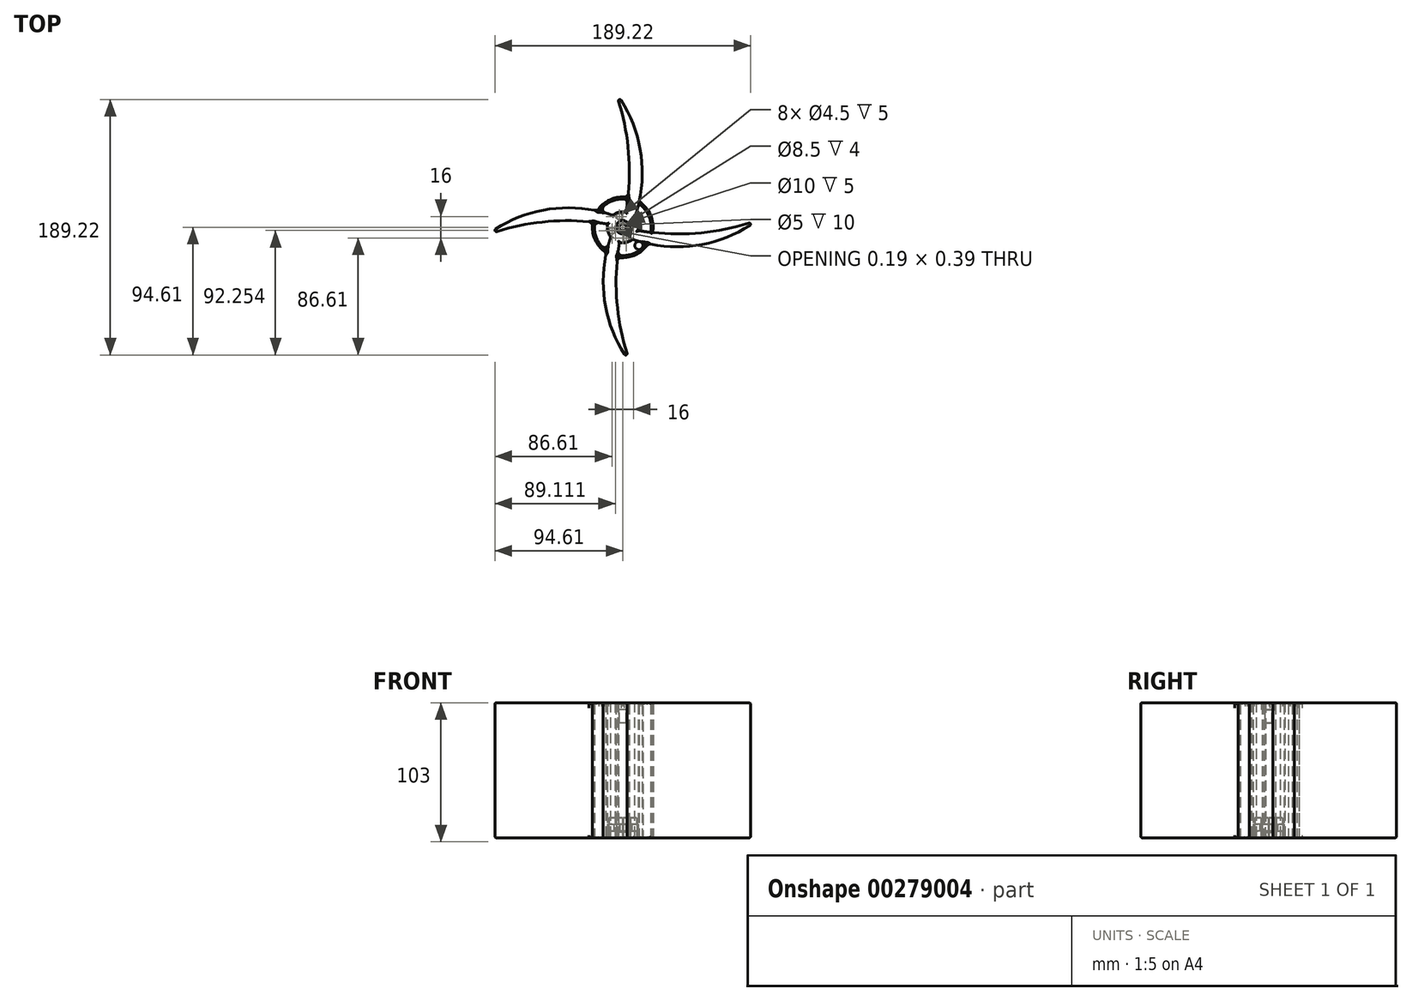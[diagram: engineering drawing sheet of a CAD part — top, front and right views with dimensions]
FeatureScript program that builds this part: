
annotation { "Feature Type Name" : "Feature", "Feature Type Description" : "" }
export const myFeature = defineFeature(function(context is Context, id is Id, definition is map)
    precondition{}
    {
        {
            assignVariable(context, id + "F0", {"name" : "BearingThickness", "anyValue" : 5});
        }
        {
            var Q0;
            Q0=qCreatedBy(makeId("Top.planeOp"),FACE);
            var sketch = newSketch(context, id + "F1", { "sketchPlane" : qUnion([Q0])});
            skCircle(sketch, "E0", {"center": v(0, 0) * mm, "radius": 2.5 * mm});
            skCircle(sketch, "E1", {"center": v(0, 0) * mm, "radius": 6 * mm});
            skPoint(sketch, "E2", {"position": v(-5.38, 100) * mm});
            skPoint(sketch, "E3", {"position": v(1.37, 5.84) * mm});
            skPoint(sketch, "E4.MirrorP", {"position": v(1.37, -5.84) * mm});
            skPoint(sketch, "E5", {"position": v(-6, 0) * mm});
            skPoint(sketch, "E6.MirrorP", {"position": v(6, 0) * mm});
            skArc(sketch, "E7", {"start": v(6, 0) * mm, "mid": v(14.14, 48) * mm, "end": v(-1.34, 94.15) * mm});
            skArc(sketch, "E8", {"start": v(1.37, 5.84) * mm, "mid": v(4.68, 49.86) * mm, "end": v(-3.13, 93.3) * mm});
            skArc(sketch, "E9.filletArc", {"start": v(-1.34, 94.15) * mm, "mid": v(-2.6, 94.52) * mm, "end": v(-3.13, 93.3) * mm});
            skCircle(sketch, "E10", {"center": v(0, 0) * mm, "radius": 11.5 * mm});
            skCircle(sketch, "E11", {"center": v(-8, -2.5) * mm, "radius": 2.25 * mm});
            skCircle(sketch, "E12", {"center": v(0, 0) * mm, "radius": 21 * mm});
            skCircle(sketch, "E13", {"center": v(0, 0) * mm, "radius": 22.5 * mm});
            skCircle(sketch, "E14.cCircle", {"center": v(-8, -2.5) * mm, "radius": 2.25 * mm, "construction": true});
            skLineSegment(sketch, "E14.0", {"start": v(-6.7, -4.75) * mm, "end": v(-9.3, -4.75) * mm});
            skLineSegment(sketch, "E14.3", {"start": v(-9.3, -0.25) * mm, "end": v(-6.7, -0.25) * mm});
            skLineSegment(sketch, "E14.4", {"start": v(-6.7, -0.25) * mm, "end": v(-5.4, -2.5) * mm});
            skLineSegment(sketch, "E14.5", {"start": v(-5.4, -2.5) * mm, "end": v(-6.7, -4.75) * mm});
            skPoint(sketch, "E14.0.midPoint", {"position": v(-8, -4.75) * mm});
            skLineSegment(sketch, "E15", {"start": v(-9.3, -4.75) * mm, "end": v(-22, -4.75) * mm});
            skLineSegment(sketch, "E16", {"start": v(-9.3, -0.25) * mm, "end": v(-22.5, -0.25) * mm});
            skSolve(sketch);
        }
        {
            var Q0;
            {var subQ0=sQuery(id+"F1.wireOp",EDGE,"E13");var subQ1=sQuery(id+"F1.wireOp",EDGE,"E7");var subQ2=makeQuery(id+"F1.imprint","INTERSECT",VERTEX,{"derivedFrom":[subQ1,subQ0]});Q0=makeQuery(id+"F1.imprint","IMPRINT",FACE,{"disambiguationData":[TD([[makeQuery(id+"F1.imprint","IMPRINT",EDGE,{"disambiguationData":[TD([[subQ2,1.0]])],"derivedFrom":subQ1}),-1.0]])]});}
            var Q1;
            Q1=makeQuery(id+"F1.imprint","IMPRINT",FACE,{"disambiguationData":[TD([[makeQuery(id+"F1.imprint","IMPRINT",EDGE,{"derivedFrom":sQuery(id+"F1.wireOp",EDGE,"E0")}),-1.0]])]});
            var Q2;
            {var subQ0=sQuery(id+"F1.wireOp",EDGE,"E16");var subQ1=sQuery(id+"F1.wireOp",EDGE,"E12");var subQ2=makeQuery(id+"F1.imprint","INTERSECT",VERTEX,{"derivedFrom":[subQ1,subQ0]});Q2=makeQuery(id+"F1.imprint","IMPRINT",FACE,{"disambiguationData":[TD([[makeQuery(id+"F1.imprint","IMPRINT",EDGE,{"disambiguationData":[TD([[subQ2,-1.0]])],"derivedFrom":subQ1}),-1.0]])]});}
            var Q3;
            {var subQ0=sQuery(id+"F1.wireOp",EDGE,"E13");var subQ1=sQuery(id+"F1.wireOp",EDGE,"E8");var subQ2=makeQuery(id+"F1.imprint","INTERSECT",VERTEX,{"derivedFrom":[subQ1,subQ0]});Q3=makeQuery(id+"F1.imprint","IMPRINT",FACE,{"disambiguationData":[TD([[makeQuery(id+"F1.imprint","IMPRINT",EDGE,{"disambiguationData":[TD([[subQ2,1.0]])],"derivedFrom":subQ1}),1.0]])]});}
            var Q4;
            {var subQ0=sQuery(id+"F1.wireOp",EDGE,"E13");var subQ1=sQuery(id+"F1.wireOp",EDGE,"E7");var subQ2=makeQuery(id+"F1.imprint","INTERSECT",VERTEX,{"derivedFrom":[subQ1,subQ0]});Q4=makeQuery(id+"F1.imprint","IMPRINT",FACE,{"disambiguationData":[TD([[makeQuery(id+"F1.imprint","IMPRINT",EDGE,{"disambiguationData":[TD([[subQ2,1.0]])],"derivedFrom":subQ1}),1.0]])]});}
            var Q5;
            {var subQ0=sQuery(id+"F1.wireOp",EDGE,"E7");var subQ1=sQuery(id+"F1.wireOp",EDGE,"E1");var subQ2=makeQuery(id+"F1.imprint","INTERSECT",VERTEX,{"derivedFrom":[subQ1,subQ0]});Q5=makeQuery(id+"F1.imprint","IMPRINT",FACE,{"disambiguationData":[TD([[makeQuery(id+"F1.imprint","IMPRINT",EDGE,{"disambiguationData":[TD([[subQ2,-1.0]])],"derivedFrom":subQ1}),-1.0]])]});}
            var Q6;
            {var subQ5=sQuery(id+"F1.wireOp",EDGE,"E16");var subQ6=sQuery(id+"F1.wireOp",EDGE,"E10");var subQ7=makeQuery(id+"F1.imprint","INTERSECT",VERTEX,{"derivedFrom":[subQ6,subQ5]});Q6=makeQuery(id+"F1.imprint","IMPRINT",FACE,{"disambiguationData":[TD([[makeQuery(id+"F1.imprint","IMPRINT",EDGE,{"disambiguationData":[TD([[subQ7,-1.0]])],"derivedFrom":subQ6}),1.0]])]});}
            var Q7;
            {var subQ0=sQuery(id+"F1.wireOp",EDGE,"E11");var subQ1=makeQuery(id+"F1.imprint","INTERSECT",VERTEX,{"derivedFrom":[subQ0,sQuery(id+"F1.wireOp",EDGE,"E14.3")]});Q7=makeQuery(id+"F1.imprint","IMPRINT",FACE,{"disambiguationData":[TD([[makeQuery(id+"F1.imprint","IMPRINT",EDGE,{"disambiguationData":[TD([[subQ1,1.0]])],"derivedFrom":subQ0}),1.0]])]});}
            var Q8;
            {var subQ0=sQuery(id+"F1.wireOp",EDGE,"E14.0");var subQ1=sQuery(id+"F1.wireOp",EDGE,"E11");var subQ2=makeQuery(id+"F1.imprint","INTERSECT",VERTEX,{"derivedFrom":[subQ1,subQ0]});Q8=makeQuery(id+"F1.imprint","IMPRINT",FACE,{"disambiguationData":[TD([[makeQuery(id+"F1.imprint","IMPRINT",EDGE,{"disambiguationData":[TD([[subQ2,-1.0]])],"derivedFrom":subQ1}),-1.0]])]});}
            var Q9;
            {var subQ0=sQuery(id+"F1.wireOp",EDGE,"E14.3");var subQ1=sQuery(id+"F1.wireOp",EDGE,"E11");var subQ2=makeQuery(id+"F1.imprint","INTERSECT",VERTEX,{"derivedFrom":[subQ1,subQ0]});Q9=makeQuery(id+"F1.imprint","IMPRINT",FACE,{"disambiguationData":[TD([[makeQuery(id+"F1.imprint","IMPRINT",EDGE,{"disambiguationData":[TD([[subQ2,1.0]])],"derivedFrom":subQ1}),-1.0]])]});}
            var Q10;
            {var subQ0=sQuery(id+"F1.wireOp",EDGE,"E14.4");var subQ1=sQuery(id+"F1.wireOp",EDGE,"E11");var subQ2=makeQuery(id+"F1.imprint","INTERSECT",VERTEX,{"derivedFrom":[subQ1,subQ0]});Q10=makeQuery(id+"F1.imprint","IMPRINT",FACE,{"disambiguationData":[TD([[makeQuery(id+"F1.imprint","IMPRINT",EDGE,{"disambiguationData":[TD([[subQ2,1.0]])],"derivedFrom":subQ1}),-1.0]])]});}
            var Q11;
            {var subQ11=sQuery(id+"F1.wireOp",EDGE,"E7");var subQ16=sQuery(id+"F1.wireOp",EDGE,"E1");var subQ17=makeQuery(id+"F1.imprint","INTERSECT",VERTEX,{"derivedFrom":[subQ16,subQ11]});Q11=makeQuery(id+"F1.imprint","IMPRINT",FACE,{"disambiguationData":[TD([[makeQuery(id+"F1.imprint","IMPRINT",EDGE,{"disambiguationData":[TD([[subQ17,1.0]])],"derivedFrom":subQ16}),-1.0]])]});}
            var Q12;
            {var subQ1=sQuery(id+"F1.wireOp",EDGE,"E8");var subQ5=sQuery(id+"F1.wireOp",EDGE,"E1");var subQ6=makeQuery(id+"F1.imprint","INTERSECT",VERTEX,{"derivedFrom":[subQ5,subQ1]});Q12=makeQuery(id+"F1.imprint","IMPRINT",FACE,{"disambiguationData":[TD([[makeQuery(id+"F1.imprint","IMPRINT",EDGE,{"disambiguationData":[TD([[subQ6,-1.0]])],"derivedFrom":subQ5}),-1.0]])]});}
            var Q13;
            Q13=makeQuery(id+"F1.imprint","IMPRINT",FACE,{"disambiguationData":[TD([[makeQuery(id+"F1.imprint","IMPRINT",EDGE,{"derivedFrom":sQuery(id+"F1.wireOp",EDGE,"E0")}),1.0]])]});
            extrude(context, id + "F2", {"entities" : qUnion([Q0, Q1, Q2, Q3, Q4, Q5, Q6, Q7, Q8, Q9, Q10, Q11, Q12, Q13]), "depth" : 100 * mm});
        }
        {
            var Q0;
            {var subQ0=sQuery(id+"F1.wireOp",EDGE,"E9.filletArc");Q0=makeQuery(id+"F1.imprint","IMPRINT",FACE,{"disambiguationData":[TD([[makeQuery(id+"F1.imprint","IMPRINT",EDGE,{"derivedFrom":subQ0}),1.0]])]});}
            var Q1;
            {var subQ0=sQuery(id+"F1.wireOp",EDGE,"E10");var subQ1=sQuery(id+"F1.wireOp",EDGE,"E7");var subQ2=makeQuery(id+"F1.imprint","INTERSECT",VERTEX,{"derivedFrom":[subQ1,subQ0]});Q1=makeQuery(id+"F1.imprint","IMPRINT",FACE,{"disambiguationData":[TD([[makeQuery(id+"F1.imprint","IMPRINT",EDGE,{"disambiguationData":[TD([[subQ2,-1.0]])],"derivedFrom":subQ1}),1.0]])]});}
            var Q2;
            {var subQ0=sQuery(id+"F1.wireOp",EDGE,"E7");var subQ1=sQuery(id+"F1.wireOp",EDGE,"E1");var subQ2=makeQuery(id+"F1.imprint","INTERSECT",VERTEX,{"derivedFrom":[subQ1,subQ0]});Q2=makeQuery(id+"F1.imprint","IMPRINT",FACE,{"disambiguationData":[TD([[makeQuery(id+"F1.imprint","IMPRINT",EDGE,{"disambiguationData":[TD([[subQ2,-1.0]])],"derivedFrom":subQ1}),-1.0]])]});}
            extrude(context, id + "F3", {"entities" : qUnion([Q0, Q1, Q2]), "depth" : 100 * mm});
        }
        {
            var Q0;
            Q0=makeQuery(id+"F3.opExtrude","SWEPT_BODY",BODY,{"disambiguationData":[OSD([sQuery(id+"F1.wireOp",EDGE,"E7"),sQuery(id+"F1.wireOp",EDGE,"E8"),sQuery(id+"F1.wireOp",EDGE,"E9.filletArc"),sQuery(id+"F1.wireOp",EDGE,"E13")])]});
            var Q1;
            Q1=makeQuery(id+"F3.opExtrude","SWEPT_BODY",BODY,{"disambiguationData":[OSD([sQuery(id+"F1.wireOp",EDGE,"E1"),sQuery(id+"F1.wireOp",EDGE,"E7"),sQuery(id+"F1.wireOp",EDGE,"E8"),sQuery(id+"F1.wireOp",EDGE,"E12")])]});
            var Q2;
            Q2=sQuery(id+"F1.wireOp",EDGE,"E0");
            circularPattern(context, id + "F4", {"operationType" : NewBodyOperationType.ADD, "entities" : qUnion([Q0, Q1]), "axis" : qUnion([Q2]), "angle" : 360 * degree, "instanceCount" : 4, "equalSpace" : true});
        }
        {
            var Q0;
            {var subQ0=sQuery(id+"F1.wireOp",EDGE,"E11");var subQ1=makeQuery(id+"F1.imprint","INTERSECT",VERTEX,{"derivedFrom":[subQ0,sQuery(id+"F1.wireOp",EDGE,"E14.3")]});Q0=makeQuery(id+"F1.imprint","IMPRINT",FACE,{"disambiguationData":[TD([[makeQuery(id+"F1.imprint","IMPRINT",EDGE,{"disambiguationData":[TD([[subQ1,1.0]])],"derivedFrom":subQ0}),1.0]])]});}
            extrude(context, id + "F5", {"entities" : qUnion([Q0]), "depth" : 15 * mm, "hasSecondDirection" : true, "secondDirectionOppositeDirection" : true, "secondDirectionDepth" : 15 * mm});
        }
        {
            var Q0;
            Q0=makeQuery(id+"F5.opExtrude","SWEPT_BODY",BODY,{"disambiguationData":[OSD([sQuery(id+"F1.wireOp",EDGE,"E11")])]});
            var Q1;
            Q1=makeQuery(id+"F5.opExtrude","SWEPT_BODY",BODY,{"disambiguationData":[OSD([sQuery(id+"F1.wireOp",EDGE,"E11")])]});
            var Q2;
            Q2=sQuery(id+"F1.wireOp",EDGE,"E0");
            circularPattern(context, id + "F6", {"operationType" : NewBodyOperationType.REMOVE, "entities" : qUnion([Q0, Q1]), "axis" : qUnion([Q2]), "angle" : 360 * degree, "instanceCount" : 4, "equalSpace" : true});
        }
        {
            var Q0;
            {var subQ5=sQuery(id+"F1.wireOp",EDGE,"E16");var subQ6=sQuery(id+"F1.wireOp",EDGE,"E10");var subQ7=makeQuery(id+"F1.imprint","INTERSECT",VERTEX,{"derivedFrom":[subQ6,subQ5]});Q0=makeQuery(id+"F1.imprint","IMPRINT",FACE,{"disambiguationData":[TD([[makeQuery(id+"F1.imprint","IMPRINT",EDGE,{"disambiguationData":[TD([[subQ7,-1.0]])],"derivedFrom":subQ6}),1.0]])]});}
            var Q1;
            {var subQ0=sQuery(id+"F1.wireOp",EDGE,"E14.4");var subQ1=sQuery(id+"F1.wireOp",EDGE,"E11");var subQ2=makeQuery(id+"F1.imprint","INTERSECT",VERTEX,{"derivedFrom":[subQ1,subQ0]});Q1=makeQuery(id+"F1.imprint","IMPRINT",FACE,{"disambiguationData":[TD([[makeQuery(id+"F1.imprint","IMPRINT",EDGE,{"disambiguationData":[TD([[subQ2,1.0]])],"derivedFrom":subQ1}),-1.0]])]});}
            var Q2;
            {var subQ0=sQuery(id+"F1.wireOp",EDGE,"E14.3");var subQ1=sQuery(id+"F1.wireOp",EDGE,"E11");var subQ2=makeQuery(id+"F1.imprint","INTERSECT",VERTEX,{"derivedFrom":[subQ1,subQ0]});Q2=makeQuery(id+"F1.imprint","IMPRINT",FACE,{"disambiguationData":[TD([[makeQuery(id+"F1.imprint","IMPRINT",EDGE,{"disambiguationData":[TD([[subQ2,1.0]])],"derivedFrom":subQ1}),-1.0]])]});}
            var Q3;
            {var subQ0=sQuery(id+"F1.wireOp",EDGE,"E14.0");var subQ1=sQuery(id+"F1.wireOp",EDGE,"E11");var subQ2=makeQuery(id+"F1.imprint","INTERSECT",VERTEX,{"derivedFrom":[subQ1,subQ0]});Q3=makeQuery(id+"F1.imprint","IMPRINT",FACE,{"disambiguationData":[TD([[makeQuery(id+"F1.imprint","IMPRINT",EDGE,{"disambiguationData":[TD([[subQ2,-1.0]])],"derivedFrom":subQ1}),-1.0]])]});}
            extrude(context, id + "F7", {"entities" : qUnion([Q0, Q1, Q2, Q3]), "depth" : 10 * mm, "hasSecondDirection" : true, "secondDirectionOppositeDirection" : false, "secondDirectionDepth" : 5 * mm});
        }
        {
            var Q0;
            Q0=makeQuery(id+"F7.opExtrude","SWEPT_BODY",BODY,{"disambiguationData":[OSD([sQuery(id+"F1.wireOp",EDGE,"E11"),sQuery(id+"F1.wireOp",EDGE,"E14.0"),sQuery(id+"F1.wireOp",EDGE,"E14.5")])]});
            var Q1;
            Q1=makeQuery(id+"F7.opExtrude","SWEPT_BODY",BODY,{"disambiguationData":[OSD([sQuery(id+"F1.wireOp",EDGE,"E11"),sQuery(id+"F1.wireOp",EDGE,"E14.4"),sQuery(id+"F1.wireOp",EDGE,"E14.5")])]});
            var Q2;
            Q2=makeQuery(id+"F7.opExtrude","SWEPT_BODY",BODY,{"disambiguationData":[OSD([sQuery(id+"F1.wireOp",EDGE,"E10"),sQuery(id+"F1.wireOp",EDGE,"E11"),sQuery(id+"F1.wireOp",EDGE,"E14.0"),sQuery(id+"F1.wireOp",EDGE,"E14.3"),sQuery(id+"F1.wireOp",EDGE,"E15"),sQuery(id+"F1.wireOp",EDGE,"E16")])]});
            var Q3;
            Q3=makeQuery(id+"F7.opExtrude","SWEPT_BODY",BODY,{"disambiguationData":[OSD([sQuery(id+"F1.wireOp",EDGE,"E11"),sQuery(id+"F1.wireOp",EDGE,"E14.3"),sQuery(id+"F1.wireOp",EDGE,"E14.4")])]});
            var Q4;
            Q4=sQuery(id+"F1.wireOp",EDGE,"E0");
            circularPattern(context, id + "F8", {"operationType" : NewBodyOperationType.REMOVE, "entities" : qUnion([Q0, Q1, Q2, Q3]), "axis" : qUnion([Q4]), "angle" : 360 * degree, "instanceCount" : 4, "equalSpace" : true});
        }
        {
            var Q0;
            {var subQ0=sQuery(id+"F1.wireOp",EDGE,"E8");Q0=makeQuery(id+"F4.opPattern","COPY",EDGE,{"derivedFrom":makeQuery(id+"F3.opExtrude","CAP_EDGE",EDGE,{"disambiguationData":[OSD([subQ0]),TDD([makeQuery(id+"F1.imprint","IMPRINT",EDGE,{"disambiguationData":[TD([[makeQuery(id+"F1.imprint","INTERSECT",VERTEX,{"derivedFrom":[subQ0,sQuery(id+"F1.wireOp",EDGE,"E9.filletArc")]}),1.0]])],"derivedFrom":subQ0})])],"isStart":true}),"instanceName":"2"});}
            var Q1;
            {var subQ0=sQuery(id+"F1.wireOp",EDGE,"E13");var subQ1=sQuery(id+"F1.wireOp",EDGE,"E9.filletArc");var subQ2=sQuery(id+"F1.wireOp",EDGE,"E8");Q1=makeQuery(id+"F4.boolean.opBoolean","SPLIT",EDGE,{"disambiguationData":[TD([makeQuery(id+"F4.opPattern","COPY",FACE,{"derivedFrom":makeQuery(id+"F3.opExtrude","SWEPT_FACE",FACE,{"disambiguationData":[OSD([subQ2]),TDD([makeQuery(id+"F1.imprint","IMPRINT",EDGE,{"disambiguationData":[TD([[makeQuery(id+"F1.imprint","INTERSECT",VERTEX,{"derivedFrom":[subQ2,subQ1]}),1.0]])],"derivedFrom":subQ2})])]}),"instanceName":"2"})])],"derivedFrom":makeQuery(id+"F2.opExtrude","CAP_EDGE",EDGE,{"disambiguationData":[OSD([subQ0])],"isStart":true})});}
            var Q2;
            {var subQ0=sQuery(id+"F1.wireOp",EDGE,"E7");Q2=makeQuery(id+"F4.opPattern","COPY",EDGE,{"derivedFrom":makeQuery(id+"F3.opExtrude","CAP_EDGE",EDGE,{"disambiguationData":[OSD([subQ0]),TDD([makeQuery(id+"F1.imprint","IMPRINT",EDGE,{"disambiguationData":[TD([[makeQuery(id+"F1.imprint","INTERSECT",VERTEX,{"derivedFrom":[subQ0,sQuery(id+"F1.wireOp",EDGE,"E9.filletArc")]}),1.0]])],"derivedFrom":subQ0})])],"isStart":true}),"instanceName":"3"});}
            var Q3;
            {var subQ0=sQuery(id+"F1.wireOp",EDGE,"E13");var subQ1=sQuery(id+"F1.wireOp",EDGE,"E9.filletArc");var subQ2=sQuery(id+"F1.wireOp",EDGE,"E8");Q3=makeQuery(id+"F4.boolean.opBoolean","SPLIT",EDGE,{"disambiguationData":[TD([makeQuery(id+"F3.opExtrude","SWEPT_FACE",FACE,{"disambiguationData":[OSD([subQ2]),TDD([makeQuery(id+"F1.imprint","IMPRINT",EDGE,{"disambiguationData":[TD([[makeQuery(id+"F1.imprint","INTERSECT",VERTEX,{"derivedFrom":[subQ2,subQ1]}),1.0]])],"derivedFrom":subQ2})])]})])],"derivedFrom":makeQuery(id+"F2.opExtrude","CAP_EDGE",EDGE,{"disambiguationData":[OSD([subQ0])],"isStart":true})});}
            var Q4;
            {var subQ0=sQuery(id+"F1.wireOp",EDGE,"E9.filletArc");var subQ2=sQuery(id+"F1.wireOp",EDGE,"E13");var subQ3=sQuery(id+"F1.wireOp",EDGE,"E8");Q4=makeQuery(id+"F4.boolean.opBoolean","SPLIT",EDGE,{"disambiguationData":[TD([makeQuery(id+"F4.opPattern","COPY",FACE,{"derivedFrom":makeQuery(id+"F3.opExtrude","SWEPT_FACE",FACE,{"disambiguationData":[OSD([subQ3]),TDD([makeQuery(id+"F1.imprint","IMPRINT",EDGE,{"disambiguationData":[TD([[makeQuery(id+"F1.imprint","INTERSECT",VERTEX,{"derivedFrom":[subQ3,subQ0]}),1.0]])],"derivedFrom":subQ3})])]}),"instanceName":"1"})])],"derivedFrom":makeQuery(id+"F2.opExtrude","CAP_EDGE",EDGE,{"disambiguationData":[OSD([subQ2])],"isStart":true})});}
            var Q5;
            {var subQ0=sQuery(id+"F1.wireOp",EDGE,"E13");var subQ1=sQuery(id+"F1.wireOp",EDGE,"E9.filletArc");var subQ3=sQuery(id+"F1.wireOp",EDGE,"E7");Q5=makeQuery(id+"F4.boolean.opBoolean","SPLIT",EDGE,{"disambiguationData":[TD([makeQuery(id+"F3.opExtrude","SWEPT_FACE",FACE,{"disambiguationData":[OSD([subQ3]),TDD([makeQuery(id+"F1.imprint","IMPRINT",EDGE,{"disambiguationData":[TD([[makeQuery(id+"F1.imprint","INTERSECT",VERTEX,{"derivedFrom":[subQ3,subQ1]}),1.0]])],"derivedFrom":subQ3})])]})])],"derivedFrom":makeQuery(id+"F2.opExtrude","CAP_EDGE",EDGE,{"disambiguationData":[OSD([subQ0])],"isStart":true})});}
            var Q6;
            {var subQ0=sQuery(id+"F1.wireOp",EDGE,"E8");Q6=makeQuery(id+"F3.opExtrude","CAP_EDGE",EDGE,{"disambiguationData":[OSD([subQ0]),TDD([makeQuery(id+"F1.imprint","IMPRINT",EDGE,{"disambiguationData":[TD([[makeQuery(id+"F1.imprint","INTERSECT",VERTEX,{"derivedFrom":[subQ0,sQuery(id+"F1.wireOp",EDGE,"E9.filletArc")]}),1.0]])],"derivedFrom":subQ0})])],"isStart":true});}
            var Q7;
            {var subQ0=sQuery(id+"F1.wireOp",EDGE,"E8");Q7=makeQuery(id+"F4.opPattern","COPY",EDGE,{"derivedFrom":makeQuery(id+"F3.opExtrude","CAP_EDGE",EDGE,{"disambiguationData":[OSD([subQ0]),TDD([makeQuery(id+"F1.imprint","IMPRINT",EDGE,{"disambiguationData":[TD([[makeQuery(id+"F1.imprint","INTERSECT",VERTEX,{"derivedFrom":[subQ0,sQuery(id+"F1.wireOp",EDGE,"E9.filletArc")]}),1.0]])],"derivedFrom":subQ0})])],"isStart":true}),"instanceName":"1"});}
            var Q8;
            {var subQ0=sQuery(id+"F1.wireOp",EDGE,"E7");var subQ1=makeQuery(id+"F1.imprint","INTERSECT",VERTEX,{"derivedFrom":[subQ0,sQuery(id+"F1.wireOp",EDGE,"E10")]});Q8=makeQuery(id+"F4.opPattern","COPY",EDGE,{"derivedFrom":makeQuery(id+"F3.opExtrude","CAP_EDGE",EDGE,{"disambiguationData":[OSD([subQ0]),TDD([makeQuery(id+"F1.imprint","IMPRINT",EDGE,{"disambiguationData":[TD([[makeQuery(id+"F1.imprint","INTERSECT",VERTEX,{"derivedFrom":[sQuery(id+"F1.wireOp",EDGE,"E1"),subQ0]}),-1.0]])],"derivedFrom":subQ0}),makeQuery(id+"F1.imprint","IMPRINT",EDGE,{"disambiguationData":[TD([[subQ1,-1.0]])],"derivedFrom":subQ0})])],"isStart":true}),"instanceName":"1"});}
            var Q9;
            {var subQ0=sQuery(id+"F1.wireOp",EDGE,"E8");var subQ1=makeQuery(id+"F1.imprint","INTERSECT",VERTEX,{"derivedFrom":[subQ0,sQuery(id+"F1.wireOp",EDGE,"E10")]});Q9=makeQuery(id+"F4.opPattern","COPY",EDGE,{"derivedFrom":makeQuery(id+"F3.opExtrude","CAP_EDGE",EDGE,{"disambiguationData":[OSD([subQ0]),TDD([makeQuery(id+"F1.imprint","IMPRINT",EDGE,{"disambiguationData":[TD([[makeQuery(id+"F1.imprint","INTERSECT",VERTEX,{"derivedFrom":[sQuery(id+"F1.wireOp",EDGE,"E1"),subQ0]}),-1.0]])],"derivedFrom":subQ0}),makeQuery(id+"F1.imprint","IMPRINT",EDGE,{"disambiguationData":[TD([[subQ1,-1.0]])],"derivedFrom":subQ0})])],"isStart":true}),"instanceName":"1"});}
            var Q10;
            {var subQ0=sQuery(id+"F1.wireOp",EDGE,"E7");var subQ1=makeQuery(id+"F1.imprint","INTERSECT",VERTEX,{"derivedFrom":[subQ0,sQuery(id+"F1.wireOp",EDGE,"E10")]});Q10=makeQuery(id+"F4.opPattern","COPY",EDGE,{"derivedFrom":makeQuery(id+"F3.opExtrude","CAP_EDGE",EDGE,{"disambiguationData":[OSD([subQ0]),TDD([makeQuery(id+"F1.imprint","IMPRINT",EDGE,{"disambiguationData":[TD([[makeQuery(id+"F1.imprint","INTERSECT",VERTEX,{"derivedFrom":[sQuery(id+"F1.wireOp",EDGE,"E1"),subQ0]}),-1.0]])],"derivedFrom":subQ0}),makeQuery(id+"F1.imprint","IMPRINT",EDGE,{"disambiguationData":[TD([[subQ1,-1.0]])],"derivedFrom":subQ0})])],"isStart":true}),"instanceName":"2"});}
            var Q11;
            {var subQ0=sQuery(id+"F1.wireOp",EDGE,"E8");var subQ1=makeQuery(id+"F1.imprint","INTERSECT",VERTEX,{"derivedFrom":[subQ0,sQuery(id+"F1.wireOp",EDGE,"E10")]});Q11=makeQuery(id+"F4.opPattern","COPY",EDGE,{"derivedFrom":makeQuery(id+"F3.opExtrude","CAP_EDGE",EDGE,{"disambiguationData":[OSD([subQ0]),TDD([makeQuery(id+"F1.imprint","IMPRINT",EDGE,{"disambiguationData":[TD([[makeQuery(id+"F1.imprint","INTERSECT",VERTEX,{"derivedFrom":[sQuery(id+"F1.wireOp",EDGE,"E1"),subQ0]}),-1.0]])],"derivedFrom":subQ0}),makeQuery(id+"F1.imprint","IMPRINT",EDGE,{"disambiguationData":[TD([[subQ1,-1.0]])],"derivedFrom":subQ0})])],"isStart":true}),"instanceName":"2"});}
            var Q12;
            {var subQ0=sQuery(id+"F1.wireOp",EDGE,"E7");var subQ1=makeQuery(id+"F1.imprint","INTERSECT",VERTEX,{"derivedFrom":[subQ0,sQuery(id+"F1.wireOp",EDGE,"E10")]});Q12=makeQuery(id+"F4.opPattern","COPY",EDGE,{"derivedFrom":makeQuery(id+"F3.opExtrude","CAP_EDGE",EDGE,{"disambiguationData":[OSD([subQ0]),TDD([makeQuery(id+"F1.imprint","IMPRINT",EDGE,{"disambiguationData":[TD([[makeQuery(id+"F1.imprint","INTERSECT",VERTEX,{"derivedFrom":[sQuery(id+"F1.wireOp",EDGE,"E1"),subQ0]}),-1.0]])],"derivedFrom":subQ0}),makeQuery(id+"F1.imprint","IMPRINT",EDGE,{"disambiguationData":[TD([[subQ1,-1.0]])],"derivedFrom":subQ0})])],"isStart":true}),"instanceName":"3"});}
            var Q13;
            {var subQ0=sQuery(id+"F1.wireOp",EDGE,"E8");var subQ1=makeQuery(id+"F1.imprint","INTERSECT",VERTEX,{"derivedFrom":[subQ0,sQuery(id+"F1.wireOp",EDGE,"E10")]});Q13=makeQuery(id+"F4.opPattern","COPY",EDGE,{"derivedFrom":makeQuery(id+"F3.opExtrude","CAP_EDGE",EDGE,{"disambiguationData":[OSD([subQ0]),TDD([makeQuery(id+"F1.imprint","IMPRINT",EDGE,{"disambiguationData":[TD([[makeQuery(id+"F1.imprint","INTERSECT",VERTEX,{"derivedFrom":[sQuery(id+"F1.wireOp",EDGE,"E1"),subQ0]}),-1.0]])],"derivedFrom":subQ0}),makeQuery(id+"F1.imprint","IMPRINT",EDGE,{"disambiguationData":[TD([[subQ1,-1.0]])],"derivedFrom":subQ0})])],"isStart":true}),"instanceName":"3"});}
            var Q14;
            {var subQ0=sQuery(id+"F1.wireOp",EDGE,"E7");var subQ1=makeQuery(id+"F1.imprint","INTERSECT",VERTEX,{"derivedFrom":[subQ0,sQuery(id+"F1.wireOp",EDGE,"E10")]});Q14=makeQuery(id+"F3.opExtrude","CAP_EDGE",EDGE,{"disambiguationData":[OSD([subQ0]),TDD([makeQuery(id+"F1.imprint","IMPRINT",EDGE,{"disambiguationData":[TD([[makeQuery(id+"F1.imprint","INTERSECT",VERTEX,{"derivedFrom":[sQuery(id+"F1.wireOp",EDGE,"E1"),subQ0]}),-1.0]])],"derivedFrom":subQ0}),makeQuery(id+"F1.imprint","IMPRINT",EDGE,{"disambiguationData":[TD([[subQ1,-1.0]])],"derivedFrom":subQ0})])],"isStart":true});}
            var Q15;
            {var subQ0=sQuery(id+"F1.wireOp",EDGE,"E8");var subQ1=makeQuery(id+"F1.imprint","INTERSECT",VERTEX,{"derivedFrom":[subQ0,sQuery(id+"F1.wireOp",EDGE,"E10")]});Q15=makeQuery(id+"F3.opExtrude","CAP_EDGE",EDGE,{"disambiguationData":[OSD([subQ0]),TDD([makeQuery(id+"F1.imprint","IMPRINT",EDGE,{"disambiguationData":[TD([[makeQuery(id+"F1.imprint","INTERSECT",VERTEX,{"derivedFrom":[sQuery(id+"F1.wireOp",EDGE,"E1"),subQ0]}),-1.0]])],"derivedFrom":subQ0}),makeQuery(id+"F1.imprint","IMPRINT",EDGE,{"disambiguationData":[TD([[subQ1,-1.0]])],"derivedFrom":subQ0})])],"isStart":true});}
            var Q16;
            {var subQ1=sQuery(id+"F1.wireOp",EDGE,"E8");var subQ4=sQuery(id+"F1.wireOp",EDGE,"E10");var subQ7=sQuery(id+"F1.wireOp",EDGE,"E1");var subQ8=makeQuery(id+"F1.imprint","INTERSECT",VERTEX,{"derivedFrom":[subQ1,subQ4]});Q16=makeQuery(id+"F4.boolean.opBoolean","SPLIT",EDGE,{"disambiguationData":[TD([makeQuery(id+"F3.opExtrude","SWEPT_FACE",FACE,{"disambiguationData":[OSD([subQ1]),TDD([makeQuery(id+"F1.imprint","IMPRINT",EDGE,{"disambiguationData":[TD([[makeQuery(id+"F1.imprint","INTERSECT",VERTEX,{"derivedFrom":[subQ7,subQ1]}),-1.0]])],"derivedFrom":subQ1}),makeQuery(id+"F1.imprint","IMPRINT",EDGE,{"disambiguationData":[TD([[subQ8,-1.0]])],"derivedFrom":subQ1})])]})])],"derivedFrom":makeQuery(id+"F2.opExtrude","CAP_EDGE",EDGE,{"disambiguationData":[OSD([subQ4])],"isStart":true})});}
            var Q17;
            {var subQ2=sQuery(id+"F1.wireOp",EDGE,"E7");var subQ4=sQuery(id+"F1.wireOp",EDGE,"E10");var subQ5=makeQuery(id+"F1.imprint","INTERSECT",VERTEX,{"derivedFrom":[subQ2,subQ4]});var subQ7=sQuery(id+"F1.wireOp",EDGE,"E1");Q17=makeQuery(id+"F4.boolean.opBoolean","SPLIT",EDGE,{"disambiguationData":[TD([makeQuery(id+"F3.opExtrude","SWEPT_FACE",FACE,{"disambiguationData":[OSD([subQ2]),TDD([makeQuery(id+"F1.imprint","IMPRINT",EDGE,{"disambiguationData":[TD([[makeQuery(id+"F1.imprint","INTERSECT",VERTEX,{"derivedFrom":[subQ7,subQ2]}),-1.0]])],"derivedFrom":subQ2}),makeQuery(id+"F1.imprint","IMPRINT",EDGE,{"disambiguationData":[TD([[subQ5,-1.0]])],"derivedFrom":subQ2})])]})])],"derivedFrom":makeQuery(id+"F2.opExtrude","CAP_EDGE",EDGE,{"disambiguationData":[OSD([subQ4])],"isStart":true})});}
            var Q18;
            {var subQ0=sQuery(id+"F1.wireOp",EDGE,"E10");var subQ1=sQuery(id+"F1.wireOp",EDGE,"E8");var subQ2=makeQuery(id+"F1.imprint","INTERSECT",VERTEX,{"derivedFrom":[subQ1,subQ0]});var subQ4=sQuery(id+"F1.wireOp",EDGE,"E1");Q18=makeQuery(id+"F4.boolean.opBoolean","SPLIT",EDGE,{"disambiguationData":[TD([makeQuery(id+"F4.opPattern","COPY",FACE,{"derivedFrom":makeQuery(id+"F3.opExtrude","SWEPT_FACE",FACE,{"disambiguationData":[OSD([subQ1]),TDD([makeQuery(id+"F1.imprint","IMPRINT",EDGE,{"disambiguationData":[TD([[makeQuery(id+"F1.imprint","INTERSECT",VERTEX,{"derivedFrom":[subQ4,subQ1]}),-1.0]])],"derivedFrom":subQ1}),makeQuery(id+"F1.imprint","IMPRINT",EDGE,{"disambiguationData":[TD([[subQ2,-1.0]])],"derivedFrom":subQ1})])]}),"instanceName":"2"})])],"derivedFrom":makeQuery(id+"F2.opExtrude","CAP_EDGE",EDGE,{"disambiguationData":[OSD([subQ0])],"isStart":true})});}
            var Q19;
            {var subQ1=sQuery(id+"F1.wireOp",EDGE,"E8");var subQ4=sQuery(id+"F1.wireOp",EDGE,"E10");var subQ7=sQuery(id+"F1.wireOp",EDGE,"E1");var subQ9=makeQuery(id+"F1.imprint","INTERSECT",VERTEX,{"derivedFrom":[subQ1,subQ4]});Q19=makeQuery(id+"F4.boolean.opBoolean","SPLIT",EDGE,{"disambiguationData":[TD([makeQuery(id+"F4.opPattern","COPY",FACE,{"derivedFrom":makeQuery(id+"F3.opExtrude","SWEPT_FACE",FACE,{"disambiguationData":[OSD([subQ1]),TDD([makeQuery(id+"F1.imprint","IMPRINT",EDGE,{"disambiguationData":[TD([[makeQuery(id+"F1.imprint","INTERSECT",VERTEX,{"derivedFrom":[subQ7,subQ1]}),-1.0]])],"derivedFrom":subQ1}),makeQuery(id+"F1.imprint","IMPRINT",EDGE,{"disambiguationData":[TD([[subQ9,-1.0]])],"derivedFrom":subQ1})])]}),"instanceName":"1"})])],"derivedFrom":makeQuery(id+"F2.opExtrude","CAP_EDGE",EDGE,{"disambiguationData":[OSD([subQ4])],"isStart":true})});}
            var Q20;
            Q20=makeQuery(id+"F8.boolean.opBoolean","COPY",EDGE,{"derivedFrom":makeQuery(id+"F8.opPattern","COPY",EDGE,{"derivedFrom":makeQuery(id+"F7.opExtrude","SWEPT_EDGE",EDGE,{"disambiguationData":[OSD([sQuery(id+"F1.wireOp",EDGE,"E10"),sQuery(id+"F1.wireOp",EDGE,"E16")])]}),"instanceName":"2"})});
            var Q21;
            Q21=makeQuery(id+"F8.boolean.opBoolean","COPY",EDGE,{"derivedFrom":makeQuery(id+"F8.opPattern","COPY",EDGE,{"derivedFrom":makeQuery(id+"F7.opExtrude","CAP_EDGE",EDGE,{"disambiguationData":[OSD([sQuery(id+"F1.wireOp",EDGE,"E10")])],"isStart":false}),"instanceName":"2"})});
            var Q22;
            Q22=makeQuery(id+"F8.boolean.opBoolean","COPY",EDGE,{"derivedFrom":makeQuery(id+"F8.opPattern","COPY",EDGE,{"derivedFrom":makeQuery(id+"F7.opExtrude","SWEPT_EDGE",EDGE,{"disambiguationData":[OSD([sQuery(id+"F1.wireOp",EDGE,"E10"),sQuery(id+"F1.wireOp",EDGE,"E15")])]}),"instanceName":"2"})});
            var Q23;
            Q23=makeQuery(id+"F8.boolean.opBoolean","COPY",EDGE,{"derivedFrom":makeQuery(id+"F8.opPattern","COPY",EDGE,{"derivedFrom":makeQuery(id+"F7.opExtrude","SWEPT_EDGE",EDGE,{"disambiguationData":[OSD([sQuery(id+"F1.wireOp",EDGE,"E10"),sQuery(id+"F1.wireOp",EDGE,"E15")])]}),"instanceName":"3"})});
            var Q24;
            Q24=makeQuery(id+"F8.boolean.opBoolean","COPY",EDGE,{"derivedFrom":makeQuery(id+"F8.opPattern","COPY",EDGE,{"derivedFrom":makeQuery(id+"F7.opExtrude","SWEPT_EDGE",EDGE,{"disambiguationData":[OSD([sQuery(id+"F1.wireOp",EDGE,"E10"),sQuery(id+"F1.wireOp",EDGE,"E16")])]}),"instanceName":"3"})});
            var Q25;
            Q25=makeQuery(id+"F8.boolean.opBoolean","COPY",EDGE,{"derivedFrom":makeQuery(id+"F8.opPattern","COPY",EDGE,{"derivedFrom":makeQuery(id+"F7.opExtrude","CAP_EDGE",EDGE,{"disambiguationData":[OSD([sQuery(id+"F1.wireOp",EDGE,"E10")])],"isStart":false}),"instanceName":"3"})});
            var Q26;
            Q26=makeQuery(id+"F8.boolean.opBoolean","COPY",EDGE,{"derivedFrom":makeQuery(id+"F7.opExtrude","CAP_EDGE",EDGE,{"disambiguationData":[OSD([sQuery(id+"F1.wireOp",EDGE,"E10")])],"isStart":false})});
            var Q27;
            Q27=makeQuery(id+"F8.boolean.opBoolean","COPY",EDGE,{"derivedFrom":makeQuery(id+"F7.opExtrude","SWEPT_EDGE",EDGE,{"disambiguationData":[OSD([sQuery(id+"F1.wireOp",EDGE,"E10"),sQuery(id+"F1.wireOp",EDGE,"E15")])]})});
            var Q28;
            Q28=makeQuery(id+"F8.boolean.opBoolean","COPY",EDGE,{"derivedFrom":makeQuery(id+"F7.opExtrude","SWEPT_EDGE",EDGE,{"disambiguationData":[OSD([sQuery(id+"F1.wireOp",EDGE,"E10"),sQuery(id+"F1.wireOp",EDGE,"E16")])]})});
            var Q29;
            Q29=makeQuery(id+"F8.boolean.opBoolean","COPY",EDGE,{"derivedFrom":makeQuery(id+"F8.opPattern","COPY",EDGE,{"derivedFrom":makeQuery(id+"F7.opExtrude","CAP_EDGE",EDGE,{"disambiguationData":[OSD([sQuery(id+"F1.wireOp",EDGE,"E10")])],"isStart":false}),"instanceName":"1"})});
            var Q30;
            Q30=makeQuery(id+"F8.boolean.opBoolean","COPY",EDGE,{"derivedFrom":makeQuery(id+"F8.opPattern","COPY",EDGE,{"derivedFrom":makeQuery(id+"F7.opExtrude","SWEPT_EDGE",EDGE,{"disambiguationData":[OSD([sQuery(id+"F1.wireOp",EDGE,"E10"),sQuery(id+"F1.wireOp",EDGE,"E15")])]}),"instanceName":"1"})});
            var Q31;
            Q31=makeQuery(id+"F8.boolean.opBoolean","COPY",EDGE,{"derivedFrom":makeQuery(id+"F8.opPattern","COPY",EDGE,{"derivedFrom":makeQuery(id+"F7.opExtrude","SWEPT_EDGE",EDGE,{"disambiguationData":[OSD([sQuery(id+"F1.wireOp",EDGE,"E10"),sQuery(id+"F1.wireOp",EDGE,"E16")])]}),"instanceName":"1"})});
            var Q32;
            {var subQ0=sQuery(id+"F1.wireOp",EDGE,"E8");Q32=makeQuery(id+"F4.opPattern","COPY",EDGE,{"derivedFrom":makeQuery(id+"F3.opExtrude","CAP_EDGE",EDGE,{"disambiguationData":[OSD([subQ0]),TDD([makeQuery(id+"F1.imprint","IMPRINT",EDGE,{"disambiguationData":[TD([[makeQuery(id+"F1.imprint","INTERSECT",VERTEX,{"derivedFrom":[subQ0,sQuery(id+"F1.wireOp",EDGE,"E9.filletArc")]}),1.0]])],"derivedFrom":subQ0})])],"isStart":false}),"instanceName":"2"});}
            var Q33;
            {var subQ0=sQuery(id+"F1.wireOp",EDGE,"E7");Q33=makeQuery(id+"F4.opPattern","COPY",EDGE,{"derivedFrom":makeQuery(id+"F3.opExtrude","CAP_EDGE",EDGE,{"disambiguationData":[OSD([subQ0]),TDD([makeQuery(id+"F1.imprint","IMPRINT",EDGE,{"disambiguationData":[TD([[makeQuery(id+"F1.imprint","INTERSECT",VERTEX,{"derivedFrom":[subQ0,sQuery(id+"F1.wireOp",EDGE,"E9.filletArc")]}),1.0]])],"derivedFrom":subQ0})])],"isStart":false}),"instanceName":"1"});}
            var Q34;
            {var subQ0=sQuery(id+"F1.wireOp",EDGE,"E7");Q34=makeQuery(id+"F3.opExtrude","CAP_EDGE",EDGE,{"disambiguationData":[OSD([subQ0]),TDD([makeQuery(id+"F1.imprint","IMPRINT",EDGE,{"disambiguationData":[TD([[makeQuery(id+"F1.imprint","INTERSECT",VERTEX,{"derivedFrom":[subQ0,sQuery(id+"F1.wireOp",EDGE,"E9.filletArc")]}),1.0]])],"derivedFrom":subQ0})])],"isStart":false});}
            var Q35;
            {var subQ0=sQuery(id+"F1.wireOp",EDGE,"E7");Q35=makeQuery(id+"F4.opPattern","COPY",EDGE,{"derivedFrom":makeQuery(id+"F3.opExtrude","CAP_EDGE",EDGE,{"disambiguationData":[OSD([subQ0]),TDD([makeQuery(id+"F1.imprint","IMPRINT",EDGE,{"disambiguationData":[TD([[makeQuery(id+"F1.imprint","INTERSECT",VERTEX,{"derivedFrom":[subQ0,sQuery(id+"F1.wireOp",EDGE,"E9.filletArc")]}),1.0]])],"derivedFrom":subQ0})])],"isStart":false}),"instanceName":"3"});}
            var Q36;
            {var subQ0=sQuery(id+"F1.wireOp",EDGE,"E13");var subQ1=sQuery(id+"F1.wireOp",EDGE,"E9.filletArc");var subQ3=sQuery(id+"F1.wireOp",EDGE,"E7");Q36=makeQuery(id+"F4.boolean.opBoolean","SPLIT",EDGE,{"disambiguationData":[TD([makeQuery(id+"F3.opExtrude","SWEPT_FACE",FACE,{"disambiguationData":[OSD([subQ3]),TDD([makeQuery(id+"F1.imprint","IMPRINT",EDGE,{"disambiguationData":[TD([[makeQuery(id+"F1.imprint","INTERSECT",VERTEX,{"derivedFrom":[subQ3,subQ1]}),1.0]])],"derivedFrom":subQ3})])]})])],"derivedFrom":makeQuery(id+"F2.opExtrude","CAP_EDGE",EDGE,{"disambiguationData":[OSD([subQ0])],"isStart":false})});}
            var Q37;
            {var subQ0=sQuery(id+"F1.wireOp",EDGE,"E13");var subQ1=sQuery(id+"F1.wireOp",EDGE,"E9.filletArc");var subQ2=sQuery(id+"F1.wireOp",EDGE,"E8");Q37=makeQuery(id+"F4.boolean.opBoolean","SPLIT",EDGE,{"disambiguationData":[TD([makeQuery(id+"F4.opPattern","COPY",FACE,{"derivedFrom":makeQuery(id+"F3.opExtrude","SWEPT_FACE",FACE,{"disambiguationData":[OSD([subQ2]),TDD([makeQuery(id+"F1.imprint","IMPRINT",EDGE,{"disambiguationData":[TD([[makeQuery(id+"F1.imprint","INTERSECT",VERTEX,{"derivedFrom":[subQ2,subQ1]}),1.0]])],"derivedFrom":subQ2})])]}),"instanceName":"2"})])],"derivedFrom":makeQuery(id+"F2.opExtrude","CAP_EDGE",EDGE,{"disambiguationData":[OSD([subQ0])],"isStart":false})});}
            var Q38;
            {var subQ0=sQuery(id+"F1.wireOp",EDGE,"E9.filletArc");var subQ2=sQuery(id+"F1.wireOp",EDGE,"E13");var subQ3=sQuery(id+"F1.wireOp",EDGE,"E8");Q38=makeQuery(id+"F4.boolean.opBoolean","SPLIT",EDGE,{"disambiguationData":[TD([makeQuery(id+"F4.opPattern","COPY",FACE,{"derivedFrom":makeQuery(id+"F3.opExtrude","SWEPT_FACE",FACE,{"disambiguationData":[OSD([subQ3]),TDD([makeQuery(id+"F1.imprint","IMPRINT",EDGE,{"disambiguationData":[TD([[makeQuery(id+"F1.imprint","INTERSECT",VERTEX,{"derivedFrom":[subQ3,subQ0]}),1.0]])],"derivedFrom":subQ3})])]}),"instanceName":"1"})])],"derivedFrom":makeQuery(id+"F2.opExtrude","CAP_EDGE",EDGE,{"disambiguationData":[OSD([subQ2])],"isStart":false})});}
            var Q39;
            {var subQ0=sQuery(id+"F1.wireOp",EDGE,"E13");var subQ1=sQuery(id+"F1.wireOp",EDGE,"E9.filletArc");var subQ2=sQuery(id+"F1.wireOp",EDGE,"E8");Q39=makeQuery(id+"F4.boolean.opBoolean","SPLIT",EDGE,{"disambiguationData":[TD([makeQuery(id+"F3.opExtrude","SWEPT_FACE",FACE,{"disambiguationData":[OSD([subQ2]),TDD([makeQuery(id+"F1.imprint","IMPRINT",EDGE,{"disambiguationData":[TD([[makeQuery(id+"F1.imprint","INTERSECT",VERTEX,{"derivedFrom":[subQ2,subQ1]}),1.0]])],"derivedFrom":subQ2})])]})])],"derivedFrom":makeQuery(id+"F2.opExtrude","CAP_EDGE",EDGE,{"disambiguationData":[OSD([subQ0])],"isStart":false})});}
            var Q40;
            {var subQ2=sQuery(id+"F1.wireOp",EDGE,"E7");var subQ4=sQuery(id+"F1.wireOp",EDGE,"E10");var subQ5=sQuery(id+"F1.wireOp",EDGE,"E12");var subQ6=sQuery(id+"F1.wireOp",EDGE,"E1");var subQ8=makeQuery(id+"F1.imprint","INTERSECT",VERTEX,{"derivedFrom":[subQ2,subQ4]});Q40=makeQuery(id+"F4.boolean.opBoolean","SPLIT",EDGE,{"disambiguationData":[TD([makeQuery(id+"F3.opExtrude","SWEPT_FACE",FACE,{"disambiguationData":[OSD([subQ2]),TDD([makeQuery(id+"F1.imprint","IMPRINT",EDGE,{"disambiguationData":[TD([[makeQuery(id+"F1.imprint","INTERSECT",VERTEX,{"derivedFrom":[subQ6,subQ2]}),-1.0]])],"derivedFrom":subQ2}),makeQuery(id+"F1.imprint","IMPRINT",EDGE,{"disambiguationData":[TD([[subQ8,-1.0]])],"derivedFrom":subQ2})])]})])],"derivedFrom":makeQuery(id+"F2.opExtrude","CAP_EDGE",EDGE,{"disambiguationData":[OSD([subQ5])],"isStart":false})});}
            var Q41;
            {var subQ0=sQuery(id+"F1.wireOp",EDGE,"E10");var subQ1=sQuery(id+"F1.wireOp",EDGE,"E8");var subQ2=makeQuery(id+"F1.imprint","INTERSECT",VERTEX,{"derivedFrom":[subQ1,subQ0]});var subQ3=sQuery(id+"F1.wireOp",EDGE,"E12");var subQ4=sQuery(id+"F1.wireOp",EDGE,"E1");Q41=makeQuery(id+"F4.boolean.opBoolean","SPLIT",EDGE,{"disambiguationData":[TD([makeQuery(id+"F4.opPattern","COPY",FACE,{"derivedFrom":makeQuery(id+"F3.opExtrude","SWEPT_FACE",FACE,{"disambiguationData":[OSD([subQ1]),TDD([makeQuery(id+"F1.imprint","IMPRINT",EDGE,{"disambiguationData":[TD([[makeQuery(id+"F1.imprint","INTERSECT",VERTEX,{"derivedFrom":[subQ4,subQ1]}),-1.0]])],"derivedFrom":subQ1}),makeQuery(id+"F1.imprint","IMPRINT",EDGE,{"disambiguationData":[TD([[subQ2,-1.0]])],"derivedFrom":subQ1})])]}),"instanceName":"2"})])],"derivedFrom":makeQuery(id+"F2.opExtrude","CAP_EDGE",EDGE,{"disambiguationData":[OSD([subQ3])],"isStart":false})});}
            var Q42;
            {var subQ0=sQuery(id+"F1.wireOp",EDGE,"E10");var subQ1=sQuery(id+"F1.wireOp",EDGE,"E8");var subQ2=makeQuery(id+"F1.imprint","INTERSECT",VERTEX,{"derivedFrom":[subQ1,subQ0]});var subQ3=sQuery(id+"F1.wireOp",EDGE,"E12");var subQ4=sQuery(id+"F1.wireOp",EDGE,"E1");Q42=makeQuery(id+"F4.boolean.opBoolean","SPLIT",EDGE,{"disambiguationData":[TD([makeQuery(id+"F4.opPattern","COPY",FACE,{"derivedFrom":makeQuery(id+"F3.opExtrude","SWEPT_FACE",FACE,{"disambiguationData":[OSD([subQ1]),TDD([makeQuery(id+"F1.imprint","IMPRINT",EDGE,{"disambiguationData":[TD([[makeQuery(id+"F1.imprint","INTERSECT",VERTEX,{"derivedFrom":[subQ4,subQ1]}),-1.0]])],"derivedFrom":subQ1}),makeQuery(id+"F1.imprint","IMPRINT",EDGE,{"disambiguationData":[TD([[subQ2,-1.0]])],"derivedFrom":subQ1})])]}),"instanceName":"1"})])],"derivedFrom":makeQuery(id+"F2.opExtrude","CAP_EDGE",EDGE,{"disambiguationData":[OSD([subQ3])],"isStart":false})});}
            var Q43;
            {var subQ1=sQuery(id+"F1.wireOp",EDGE,"E8");var subQ4=sQuery(id+"F1.wireOp",EDGE,"E10");var subQ6=sQuery(id+"F1.wireOp",EDGE,"E12");var subQ7=sQuery(id+"F1.wireOp",EDGE,"E1");var subQ9=makeQuery(id+"F1.imprint","INTERSECT",VERTEX,{"derivedFrom":[subQ1,subQ4]});Q43=makeQuery(id+"F4.boolean.opBoolean","SPLIT",EDGE,{"disambiguationData":[TD([makeQuery(id+"F3.opExtrude","SWEPT_FACE",FACE,{"disambiguationData":[OSD([subQ1]),TDD([makeQuery(id+"F1.imprint","IMPRINT",EDGE,{"disambiguationData":[TD([[makeQuery(id+"F1.imprint","INTERSECT",VERTEX,{"derivedFrom":[subQ7,subQ1]}),-1.0]])],"derivedFrom":subQ1}),makeQuery(id+"F1.imprint","IMPRINT",EDGE,{"disambiguationData":[TD([[subQ9,-1.0]])],"derivedFrom":subQ1})])]})])],"derivedFrom":makeQuery(id+"F2.opExtrude","CAP_EDGE",EDGE,{"disambiguationData":[OSD([subQ6])],"isStart":false})});}
            var Q44;
            {var subQ2=sQuery(id+"F1.wireOp",EDGE,"E7");var subQ4=sQuery(id+"F1.wireOp",EDGE,"E10");var subQ6=sQuery(id+"F1.wireOp",EDGE,"E1");var subQ8=makeQuery(id+"F1.imprint","INTERSECT",VERTEX,{"derivedFrom":[subQ2,subQ4]});Q44=makeQuery(id+"F4.boolean.opBoolean","SPLIT",EDGE,{"disambiguationData":[TD([makeQuery(id+"F3.opExtrude","SWEPT_FACE",FACE,{"disambiguationData":[OSD([subQ2]),TDD([makeQuery(id+"F1.imprint","IMPRINT",EDGE,{"disambiguationData":[TD([[makeQuery(id+"F1.imprint","INTERSECT",VERTEX,{"derivedFrom":[subQ6,subQ2]}),-1.0]])],"derivedFrom":subQ2}),makeQuery(id+"F1.imprint","IMPRINT",EDGE,{"disambiguationData":[TD([[subQ8,-1.0]])],"derivedFrom":subQ2})])]})])],"derivedFrom":makeQuery(id+"F2.opExtrude","CAP_EDGE",EDGE,{"disambiguationData":[OSD([subQ4])],"isStart":false})});}
            var Q45;
            {var subQ0=sQuery(id+"F1.wireOp",EDGE,"E8");var subQ1=makeQuery(id+"F1.imprint","INTERSECT",VERTEX,{"derivedFrom":[subQ0,sQuery(id+"F1.wireOp",EDGE,"E10")]});Q45=makeQuery(id+"F4.opPattern","COPY",EDGE,{"derivedFrom":makeQuery(id+"F3.opExtrude","CAP_EDGE",EDGE,{"disambiguationData":[OSD([subQ0]),TDD([makeQuery(id+"F1.imprint","IMPRINT",EDGE,{"disambiguationData":[TD([[makeQuery(id+"F1.imprint","INTERSECT",VERTEX,{"derivedFrom":[sQuery(id+"F1.wireOp",EDGE,"E1"),subQ0]}),-1.0]])],"derivedFrom":subQ0}),makeQuery(id+"F1.imprint","IMPRINT",EDGE,{"disambiguationData":[TD([[subQ1,-1.0]])],"derivedFrom":subQ0})])],"isStart":false}),"instanceName":"3"});}
            var Q46;
            {var subQ0=sQuery(id+"F1.wireOp",EDGE,"E7");var subQ1=makeQuery(id+"F1.imprint","INTERSECT",VERTEX,{"derivedFrom":[subQ0,sQuery(id+"F1.wireOp",EDGE,"E10")]});Q46=makeQuery(id+"F4.opPattern","COPY",EDGE,{"derivedFrom":makeQuery(id+"F3.opExtrude","CAP_EDGE",EDGE,{"disambiguationData":[OSD([subQ0]),TDD([makeQuery(id+"F1.imprint","IMPRINT",EDGE,{"disambiguationData":[TD([[makeQuery(id+"F1.imprint","INTERSECT",VERTEX,{"derivedFrom":[sQuery(id+"F1.wireOp",EDGE,"E1"),subQ0]}),-1.0]])],"derivedFrom":subQ0}),makeQuery(id+"F1.imprint","IMPRINT",EDGE,{"disambiguationData":[TD([[subQ1,-1.0]])],"derivedFrom":subQ0})])],"isStart":false}),"instanceName":"3"});}
            var Q47;
            {var subQ0=sQuery(id+"F1.wireOp",EDGE,"E7");var subQ1=makeQuery(id+"F1.imprint","INTERSECT",VERTEX,{"derivedFrom":[subQ0,sQuery(id+"F1.wireOp",EDGE,"E10")]});Q47=makeQuery(id+"F3.opExtrude","CAP_EDGE",EDGE,{"disambiguationData":[OSD([subQ0]),TDD([makeQuery(id+"F1.imprint","IMPRINT",EDGE,{"disambiguationData":[TD([[makeQuery(id+"F1.imprint","INTERSECT",VERTEX,{"derivedFrom":[sQuery(id+"F1.wireOp",EDGE,"E1"),subQ0]}),-1.0]])],"derivedFrom":subQ0}),makeQuery(id+"F1.imprint","IMPRINT",EDGE,{"disambiguationData":[TD([[subQ1,-1.0]])],"derivedFrom":subQ0})])],"isStart":false});}
            var Q48;
            {var subQ0=sQuery(id+"F1.wireOp",EDGE,"E7");var subQ1=makeQuery(id+"F1.imprint","INTERSECT",VERTEX,{"derivedFrom":[subQ0,sQuery(id+"F1.wireOp",EDGE,"E10")]});Q48=makeQuery(id+"F4.opPattern","COPY",EDGE,{"derivedFrom":makeQuery(id+"F3.opExtrude","CAP_EDGE",EDGE,{"disambiguationData":[OSD([subQ0]),TDD([makeQuery(id+"F1.imprint","IMPRINT",EDGE,{"disambiguationData":[TD([[makeQuery(id+"F1.imprint","INTERSECT",VERTEX,{"derivedFrom":[sQuery(id+"F1.wireOp",EDGE,"E1"),subQ0]}),-1.0]])],"derivedFrom":subQ0}),makeQuery(id+"F1.imprint","IMPRINT",EDGE,{"disambiguationData":[TD([[subQ1,-1.0]])],"derivedFrom":subQ0})])],"isStart":false}),"instanceName":"1"});}
            var Q49;
            {var subQ1=sQuery(id+"F1.wireOp",EDGE,"E8");var subQ4=sQuery(id+"F1.wireOp",EDGE,"E10");var subQ7=sQuery(id+"F1.wireOp",EDGE,"E1");var subQ9=makeQuery(id+"F1.imprint","INTERSECT",VERTEX,{"derivedFrom":[subQ1,subQ4]});Q49=makeQuery(id+"F4.boolean.opBoolean","SPLIT",EDGE,{"disambiguationData":[TD([makeQuery(id+"F3.opExtrude","SWEPT_FACE",FACE,{"disambiguationData":[OSD([subQ1]),TDD([makeQuery(id+"F1.imprint","IMPRINT",EDGE,{"disambiguationData":[TD([[makeQuery(id+"F1.imprint","INTERSECT",VERTEX,{"derivedFrom":[subQ7,subQ1]}),-1.0]])],"derivedFrom":subQ1}),makeQuery(id+"F1.imprint","IMPRINT",EDGE,{"disambiguationData":[TD([[subQ9,-1.0]])],"derivedFrom":subQ1})])]})])],"derivedFrom":makeQuery(id+"F2.opExtrude","CAP_EDGE",EDGE,{"disambiguationData":[OSD([subQ4])],"isStart":false})});}
            var Q50;
            {var subQ0=sQuery(id+"F1.wireOp",EDGE,"E8");var subQ1=makeQuery(id+"F1.imprint","INTERSECT",VERTEX,{"derivedFrom":[subQ0,sQuery(id+"F1.wireOp",EDGE,"E10")]});Q50=makeQuery(id+"F3.opExtrude","CAP_EDGE",EDGE,{"disambiguationData":[OSD([subQ0]),TDD([makeQuery(id+"F1.imprint","IMPRINT",EDGE,{"disambiguationData":[TD([[makeQuery(id+"F1.imprint","INTERSECT",VERTEX,{"derivedFrom":[sQuery(id+"F1.wireOp",EDGE,"E1"),subQ0]}),-1.0]])],"derivedFrom":subQ0}),makeQuery(id+"F1.imprint","IMPRINT",EDGE,{"disambiguationData":[TD([[subQ1,-1.0]])],"derivedFrom":subQ0})])],"isStart":false});}
            var Q51;
            {var subQ0=sQuery(id+"F1.wireOp",EDGE,"E10");var subQ1=sQuery(id+"F1.wireOp",EDGE,"E8");var subQ2=makeQuery(id+"F1.imprint","INTERSECT",VERTEX,{"derivedFrom":[subQ1,subQ0]});var subQ4=sQuery(id+"F1.wireOp",EDGE,"E1");Q51=makeQuery(id+"F4.boolean.opBoolean","SPLIT",EDGE,{"disambiguationData":[TD([makeQuery(id+"F4.opPattern","COPY",FACE,{"derivedFrom":makeQuery(id+"F3.opExtrude","SWEPT_FACE",FACE,{"disambiguationData":[OSD([subQ1]),TDD([makeQuery(id+"F1.imprint","IMPRINT",EDGE,{"disambiguationData":[TD([[makeQuery(id+"F1.imprint","INTERSECT",VERTEX,{"derivedFrom":[subQ4,subQ1]}),-1.0]])],"derivedFrom":subQ1}),makeQuery(id+"F1.imprint","IMPRINT",EDGE,{"disambiguationData":[TD([[subQ2,-1.0]])],"derivedFrom":subQ1})])]}),"instanceName":"2"})])],"derivedFrom":makeQuery(id+"F2.opExtrude","CAP_EDGE",EDGE,{"disambiguationData":[OSD([subQ0])],"isStart":false})});}
            var Q52;
            {var subQ0=sQuery(id+"F1.wireOp",EDGE,"E8");var subQ1=makeQuery(id+"F1.imprint","INTERSECT",VERTEX,{"derivedFrom":[subQ0,sQuery(id+"F1.wireOp",EDGE,"E10")]});Q52=makeQuery(id+"F4.opPattern","COPY",EDGE,{"derivedFrom":makeQuery(id+"F3.opExtrude","CAP_EDGE",EDGE,{"disambiguationData":[OSD([subQ0]),TDD([makeQuery(id+"F1.imprint","IMPRINT",EDGE,{"disambiguationData":[TD([[makeQuery(id+"F1.imprint","INTERSECT",VERTEX,{"derivedFrom":[sQuery(id+"F1.wireOp",EDGE,"E1"),subQ0]}),-1.0]])],"derivedFrom":subQ0}),makeQuery(id+"F1.imprint","IMPRINT",EDGE,{"disambiguationData":[TD([[subQ1,-1.0]])],"derivedFrom":subQ0})])],"isStart":false}),"instanceName":"2"});}
            var Q53;
            {var subQ0=sQuery(id+"F1.wireOp",EDGE,"E7");var subQ1=makeQuery(id+"F1.imprint","INTERSECT",VERTEX,{"derivedFrom":[subQ0,sQuery(id+"F1.wireOp",EDGE,"E10")]});Q53=makeQuery(id+"F4.opPattern","COPY",EDGE,{"derivedFrom":makeQuery(id+"F3.opExtrude","CAP_EDGE",EDGE,{"disambiguationData":[OSD([subQ0]),TDD([makeQuery(id+"F1.imprint","IMPRINT",EDGE,{"disambiguationData":[TD([[makeQuery(id+"F1.imprint","INTERSECT",VERTEX,{"derivedFrom":[sQuery(id+"F1.wireOp",EDGE,"E1"),subQ0]}),-1.0]])],"derivedFrom":subQ0}),makeQuery(id+"F1.imprint","IMPRINT",EDGE,{"disambiguationData":[TD([[subQ1,-1.0]])],"derivedFrom":subQ0})])],"isStart":false}),"instanceName":"2"});}
            var Q54;
            {var subQ1=sQuery(id+"F1.wireOp",EDGE,"E8");var subQ5=sQuery(id+"F1.wireOp",EDGE,"E1");var subQ7=sQuery(id+"F1.wireOp",EDGE,"E10");var subQ9=makeQuery(id+"F1.imprint","INTERSECT",VERTEX,{"derivedFrom":[subQ1,subQ7]});Q54=makeQuery(id+"F4.boolean.opBoolean","SPLIT",EDGE,{"disambiguationData":[TD([makeQuery(id+"F4.opPattern","COPY",FACE,{"derivedFrom":makeQuery(id+"F3.opExtrude","SWEPT_FACE",FACE,{"disambiguationData":[OSD([subQ1]),TDD([makeQuery(id+"F1.imprint","IMPRINT",EDGE,{"disambiguationData":[TD([[makeQuery(id+"F1.imprint","INTERSECT",VERTEX,{"derivedFrom":[subQ5,subQ1]}),-1.0]])],"derivedFrom":subQ1}),makeQuery(id+"F1.imprint","IMPRINT",EDGE,{"disambiguationData":[TD([[subQ9,-1.0]])],"derivedFrom":subQ1})])]}),"instanceName":"1"})])],"derivedFrom":makeQuery(id+"F2.opExtrude","CAP_EDGE",EDGE,{"disambiguationData":[OSD([subQ7])],"isStart":false})});}
            var Q55;
            {var subQ0=sQuery(id+"F1.wireOp",EDGE,"E8");var subQ1=makeQuery(id+"F1.imprint","INTERSECT",VERTEX,{"derivedFrom":[subQ0,sQuery(id+"F1.wireOp",EDGE,"E10")]});Q55=makeQuery(id+"F4.opPattern","COPY",EDGE,{"derivedFrom":makeQuery(id+"F3.opExtrude","CAP_EDGE",EDGE,{"disambiguationData":[OSD([subQ0]),TDD([makeQuery(id+"F1.imprint","IMPRINT",EDGE,{"disambiguationData":[TD([[makeQuery(id+"F1.imprint","INTERSECT",VERTEX,{"derivedFrom":[sQuery(id+"F1.wireOp",EDGE,"E1"),subQ0]}),-1.0]])],"derivedFrom":subQ0}),makeQuery(id+"F1.imprint","IMPRINT",EDGE,{"disambiguationData":[TD([[subQ1,-1.0]])],"derivedFrom":subQ0})])],"isStart":false}),"instanceName":"1"});}
            fillet(context, id + "F9", {"entities" : qUnion([Q0, Q1, Q2, Q3, Q4, Q5, Q6, Q7, Q8, Q9, Q10, Q11, Q12, Q13, Q14, Q15, Q16, Q17, Q18, Q19, Q20, Q21, Q22, Q23, Q24, Q25, Q26, Q27, Q28, Q29, Q30, Q31, Q32, Q33, Q34, Q35, Q36, Q37, Q38, Q39, Q40, Q41, Q42, Q43, Q44, Q45, Q46, Q47, Q48, Q49, Q50, Q51, Q52, Q53, Q54, Q55]), "radius" : 1 * mm, "tangentPropagation" : true, "allowEdgeOverflow" : false});
        }
        {
            var Q0;
            Q0=makeQuery(id+"F1.imprint","IMPRINT",FACE,{"disambiguationData":[TD([[makeQuery(id+"F1.imprint","IMPRINT",EDGE,{"derivedFrom":sQuery(id+"F1.wireOp",EDGE,"E0")}),-1.0]])]});
            var sketch = newSketch(context, id + "F10", { "sketchPlane" : qUnion([Q0])});
            skCircle(sketch, "E17", {"center": v(0, 0) * mm, "radius": 4.25 * mm});
            skSolve(sketch);
        }
        {
            var Q0;
            Q0 = qSketchRegion(id + "F10", true);
            var Q1;
            Q1=makeQuery(id+"F1.imprint","IMPRINT",FACE,{"disambiguationData":[TD([[makeQuery(id+"F1.imprint","IMPRINT",EDGE,{"derivedFrom":sQuery(id+"F1.wireOp",EDGE,"E0")}),1.0]])]});
            extrude(context, id + "F11", {"entities" : qUnion([Q0, Q1]), "operationType" : NewBodyOperationType.REMOVE, "depth" : 4 * mm});
        }
        {
            var Q0;
            {var subQ0=sQuery(id+"F1.wireOp",EDGE,"E13");var subQ1=sQuery(id+"F1.wireOp",EDGE,"E8");var subQ2=sQuery(id+"F1.wireOp",EDGE,"E7");var subQ3=makeQuery(id+"F3.opExtrude","CAP_FACE",FACE,{"disambiguationData":[OSD([subQ2,subQ1,sQuery(id+"F1.wireOp",EDGE,"E9.filletArc"),subQ0])],"isStart":false});var subQ4=sQuery(id+"F1.wireOp",EDGE,"E12");var subQ5=sQuery(id+"F1.wireOp",EDGE,"E1");var subQ6=makeQuery(id+"F3.opExtrude","CAP_FACE",FACE,{"disambiguationData":[OSD([subQ5,subQ2,subQ1,subQ4])],"isStart":false});Q0=makeQuery(id+"F4.boolean.opBoolean","MERGE",FACE,{"derivedFrom":[makeQuery(id+"F2.opExtrude","CAP_FACE",FACE,{"disambiguationData":[OSD([subQ5,sQuery(id+"F1.wireOp",EDGE,"E10"),sQuery(id+"F1.wireOp",EDGE,"E14.4"),sQuery(id+"F1.wireOp",EDGE,"E14.5")])],"isStart":false}),makeQuery(id+"F2.opExtrude","CAP_FACE",FACE,{"disambiguationData":[OSD([subQ4,subQ0])],"isStart":false}),subQ6,subQ3,makeQuery(id+"F4.opPattern","COPY",FACE,{"derivedFrom":subQ6,"instanceName":"1"}),makeQuery(id+"F4.opPattern","COPY",FACE,{"derivedFrom":subQ3,"instanceName":"1"}),makeQuery(id+"F4.opPattern","COPY",FACE,{"derivedFrom":subQ6,"instanceName":"2"}),makeQuery(id+"F4.opPattern","COPY",FACE,{"derivedFrom":subQ3,"instanceName":"2"}),makeQuery(id+"F4.opPattern","COPY",FACE,{"derivedFrom":subQ6,"instanceName":"3"}),makeQuery(id+"F4.opPattern","COPY",FACE,{"derivedFrom":subQ3,"instanceName":"3"})]});}
            var sketch = newSketch(context, id + "F12", { "sketchPlane" : qUnion([Q0])});
            skCircle(sketch, "E18", {"center": v(0, 0) * mm, "radius": 2.5 * mm});
            skCircle(sketch, "E19", {"center": v(0, 0) * mm, "radius": 5 * mm});
            skSolve(sketch);
        }
        {
            var Q0;
            Q0=makeQuery(id+"F12.imprint","IMPRINT",FACE,{"disambiguationData":[TD([[makeQuery(id+"F12.imprint","IMPRINT",EDGE,{"derivedFrom":sQuery(id+"F12.wireOp",EDGE,"E18")}),1.0]])]});
            extrude(context, id + "F13", {"entities" : qUnion([Q0]), "operationType" : NewBodyOperationType.REMOVE, "oppositeDirection" : true, "depth" : 15 * mm});
        }
        {
            var Q0;
            Q0=makeQuery(id+"F12.imprint","IMPRINT",FACE,{"disambiguationData":[TD([[makeQuery(id+"F12.imprint","IMPRINT",EDGE,{"derivedFrom":sQuery(id+"F12.wireOp",EDGE,"E18")}),-1.0]])]});
            extrude(context, id + "F14", {"entities" : qUnion([Q0]), "operationType" : NewBodyOperationType.REMOVE, "oppositeDirection" : true, "depth" : (getVariable(context, 'BearingThickness')) * mm});
        }
        {
            var Q0;
            Q0=makeQuery(id+"F4.opPattern","COPY",EDGE,{"derivedFrom":makeQuery(id+"F3.opExtrude","SWEPT_EDGE",EDGE,{"disambiguationData":[OSD([sQuery(id+"F1.wireOp",EDGE,"E8"),sQuery(id+"F1.wireOp",EDGE,"E13")])]}),"instanceName":"1"});
            var Q1;
            Q1=makeQuery(id+"F4.opPattern","COPY",EDGE,{"derivedFrom":makeQuery(id+"F3.opExtrude","SWEPT_EDGE",EDGE,{"disambiguationData":[OSD([sQuery(id+"F1.wireOp",EDGE,"E7"),sQuery(id+"F1.wireOp",EDGE,"E13")])]}),"instanceName":"2"});
            var Q2;
            Q2=makeQuery(id+"F4.opPattern","COPY",EDGE,{"derivedFrom":makeQuery(id+"F3.opExtrude","SWEPT_EDGE",EDGE,{"disambiguationData":[OSD([sQuery(id+"F1.wireOp",EDGE,"E8"),sQuery(id+"F1.wireOp",EDGE,"E12")])]}),"instanceName":"1"});
            var Q3;
            Q3=makeQuery(id+"F4.opPattern","COPY",EDGE,{"derivedFrom":makeQuery(id+"F3.opExtrude","SWEPT_EDGE",EDGE,{"disambiguationData":[OSD([sQuery(id+"F1.wireOp",EDGE,"E7"),sQuery(id+"F1.wireOp",EDGE,"E12")])]}),"instanceName":"2"});
            var Q4;
            Q4=makeQuery(id+"F4.opPattern","COPY",EDGE,{"derivedFrom":makeQuery(id+"F3.opExtrude","SWEPT_EDGE",EDGE,{"disambiguationData":[OSD([sQuery(id+"F1.wireOp",EDGE,"E7"),sQuery(id+"F1.wireOp",EDGE,"E12")])]}),"instanceName":"3"});
            var Q5;
            Q5=makeQuery(id+"F4.opPattern","COPY",EDGE,{"derivedFrom":makeQuery(id+"F3.opExtrude","SWEPT_EDGE",EDGE,{"disambiguationData":[OSD([sQuery(id+"F1.wireOp",EDGE,"E8"),sQuery(id+"F1.wireOp",EDGE,"E13")])]}),"instanceName":"2"});
            var Q6;
            Q6=makeQuery(id+"F4.opPattern","COPY",EDGE,{"derivedFrom":makeQuery(id+"F3.opExtrude","SWEPT_EDGE",EDGE,{"disambiguationData":[OSD([sQuery(id+"F1.wireOp",EDGE,"E7"),sQuery(id+"F1.wireOp",EDGE,"E13")])]}),"instanceName":"3"});
            var Q7;
            Q7=makeQuery(id+"F4.opPattern","COPY",EDGE,{"derivedFrom":makeQuery(id+"F3.opExtrude","SWEPT_EDGE",EDGE,{"disambiguationData":[OSD([sQuery(id+"F1.wireOp",EDGE,"E8"),sQuery(id+"F1.wireOp",EDGE,"E12")])]}),"instanceName":"2"});
            var Q8;
            Q8=makeQuery(id+"F3.opExtrude","SWEPT_EDGE",EDGE,{"disambiguationData":[OSD([sQuery(id+"F1.wireOp",EDGE,"E7"),sQuery(id+"F1.wireOp",EDGE,"E12")])]});
            var Q9;
            Q9=makeQuery(id+"F4.opPattern","COPY",EDGE,{"derivedFrom":makeQuery(id+"F3.opExtrude","SWEPT_EDGE",EDGE,{"disambiguationData":[OSD([sQuery(id+"F1.wireOp",EDGE,"E8"),sQuery(id+"F1.wireOp",EDGE,"E12")])]}),"instanceName":"3"});
            var Q10;
            Q10=makeQuery(id+"F3.opExtrude","SWEPT_EDGE",EDGE,{"disambiguationData":[OSD([sQuery(id+"F1.wireOp",EDGE,"E7"),sQuery(id+"F1.wireOp",EDGE,"E13")])]});
            var Q11;
            Q11=makeQuery(id+"F4.opPattern","COPY",EDGE,{"derivedFrom":makeQuery(id+"F3.opExtrude","SWEPT_EDGE",EDGE,{"disambiguationData":[OSD([sQuery(id+"F1.wireOp",EDGE,"E8"),sQuery(id+"F1.wireOp",EDGE,"E13")])]}),"instanceName":"3"});
            var Q12;
            Q12=makeQuery(id+"F3.opExtrude","SWEPT_EDGE",EDGE,{"disambiguationData":[OSD([sQuery(id+"F1.wireOp",EDGE,"E8"),sQuery(id+"F1.wireOp",EDGE,"E13")])]});
            var Q13;
            Q13=makeQuery(id+"F4.opPattern","COPY",EDGE,{"derivedFrom":makeQuery(id+"F3.opExtrude","SWEPT_EDGE",EDGE,{"disambiguationData":[OSD([sQuery(id+"F1.wireOp",EDGE,"E7"),sQuery(id+"F1.wireOp",EDGE,"E13")])]}),"instanceName":"1"});
            var Q14;
            Q14=makeQuery(id+"F3.opExtrude","SWEPT_EDGE",EDGE,{"disambiguationData":[OSD([sQuery(id+"F1.wireOp",EDGE,"E8"),sQuery(id+"F1.wireOp",EDGE,"E12")])]});
            var Q15;
            Q15=makeQuery(id+"F4.opPattern","COPY",EDGE,{"derivedFrom":makeQuery(id+"F3.opExtrude","SWEPT_EDGE",EDGE,{"disambiguationData":[OSD([sQuery(id+"F1.wireOp",EDGE,"E7"),sQuery(id+"F1.wireOp",EDGE,"E12")])]}),"instanceName":"1"});
            fillet(context, id + "F15", {"entities" : qUnion([Q0, Q1, Q2, Q3, Q4, Q5, Q6, Q7, Q8, Q9, Q10, Q11, Q12, Q13, Q14, Q15]), "radius" : 3 * mm, "tangentPropagation" : true, "allowEdgeOverflow" : false});
        }
        {
            var Q0;
            {var subQ0=sQuery(id+"F1.wireOp",EDGE,"E10");var subQ1=sQuery(id+"F1.wireOp",EDGE,"E7");var subQ2=makeQuery(id+"F1.imprint","INTERSECT",VERTEX,{"derivedFrom":[subQ1,subQ0]});Q0=makeQuery(id+"F4.boolean.opBoolean","INTERSECT",EDGE,{"derivedFrom":[makeQuery(id+"F2.opExtrude","SWEPT_FACE",FACE,{"disambiguationData":[OSD([subQ0])]}),makeQuery(id+"F4.opPattern","COPY",FACE,{"derivedFrom":makeQuery(id+"F3.opExtrude","SWEPT_FACE",FACE,{"disambiguationData":[OSD([subQ1]),TDD([makeQuery(id+"F1.imprint","IMPRINT",EDGE,{"disambiguationData":[TD([[makeQuery(id+"F1.imprint","INTERSECT",VERTEX,{"derivedFrom":[sQuery(id+"F1.wireOp",EDGE,"E1"),subQ1]}),-1.0]])],"derivedFrom":subQ1}),makeQuery(id+"F1.imprint","IMPRINT",EDGE,{"disambiguationData":[TD([[subQ2,-1.0]])],"derivedFrom":subQ1})])]}),"instanceName":"3"})]});}
            var Q1;
            {var subQ0=sQuery(id+"F1.wireOp",EDGE,"E10");var subQ1=sQuery(id+"F1.wireOp",EDGE,"E8");var subQ2=makeQuery(id+"F1.imprint","INTERSECT",VERTEX,{"derivedFrom":[subQ1,subQ0]});Q1=makeQuery(id+"F4.boolean.opBoolean","INTERSECT",EDGE,{"derivedFrom":[makeQuery(id+"F2.opExtrude","SWEPT_FACE",FACE,{"disambiguationData":[OSD([subQ0])]}),makeQuery(id+"F4.opPattern","COPY",FACE,{"derivedFrom":makeQuery(id+"F3.opExtrude","SWEPT_FACE",FACE,{"disambiguationData":[OSD([subQ1]),TDD([makeQuery(id+"F1.imprint","IMPRINT",EDGE,{"disambiguationData":[TD([[makeQuery(id+"F1.imprint","INTERSECT",VERTEX,{"derivedFrom":[sQuery(id+"F1.wireOp",EDGE,"E1"),subQ1]}),-1.0]])],"derivedFrom":subQ1}),makeQuery(id+"F1.imprint","IMPRINT",EDGE,{"disambiguationData":[TD([[subQ2,-1.0]])],"derivedFrom":subQ1})])]}),"instanceName":"2"})]});}
            var Q2;
            {var subQ0=sQuery(id+"F1.wireOp",EDGE,"E10");var subQ1=sQuery(id+"F1.wireOp",EDGE,"E7");var subQ2=makeQuery(id+"F1.imprint","INTERSECT",VERTEX,{"derivedFrom":[subQ1,subQ0]});Q2=makeQuery(id+"F4.boolean.opBoolean","INTERSECT",EDGE,{"derivedFrom":[makeQuery(id+"F2.opExtrude","SWEPT_FACE",FACE,{"disambiguationData":[OSD([subQ0])]}),makeQuery(id+"F3.opExtrude","SWEPT_FACE",FACE,{"disambiguationData":[OSD([subQ1]),TDD([makeQuery(id+"F1.imprint","IMPRINT",EDGE,{"disambiguationData":[TD([[makeQuery(id+"F1.imprint","INTERSECT",VERTEX,{"derivedFrom":[sQuery(id+"F1.wireOp",EDGE,"E1"),subQ1]}),-1.0]])],"derivedFrom":subQ1}),makeQuery(id+"F1.imprint","IMPRINT",EDGE,{"disambiguationData":[TD([[subQ2,-1.0]])],"derivedFrom":subQ1})])]})]});}
            var Q3;
            {var subQ0=sQuery(id+"F1.wireOp",EDGE,"E10");var subQ1=sQuery(id+"F1.wireOp",EDGE,"E8");var subQ2=makeQuery(id+"F1.imprint","INTERSECT",VERTEX,{"derivedFrom":[subQ1,subQ0]});Q3=makeQuery(id+"F4.boolean.opBoolean","INTERSECT",EDGE,{"derivedFrom":[makeQuery(id+"F2.opExtrude","SWEPT_FACE",FACE,{"disambiguationData":[OSD([subQ0])]}),makeQuery(id+"F4.opPattern","COPY",FACE,{"derivedFrom":makeQuery(id+"F3.opExtrude","SWEPT_FACE",FACE,{"disambiguationData":[OSD([subQ1]),TDD([makeQuery(id+"F1.imprint","IMPRINT",EDGE,{"disambiguationData":[TD([[makeQuery(id+"F1.imprint","INTERSECT",VERTEX,{"derivedFrom":[sQuery(id+"F1.wireOp",EDGE,"E1"),subQ1]}),-1.0]])],"derivedFrom":subQ1}),makeQuery(id+"F1.imprint","IMPRINT",EDGE,{"disambiguationData":[TD([[subQ2,-1.0]])],"derivedFrom":subQ1})])]}),"instanceName":"3"})]});}
            var Q4;
            {var subQ0=sQuery(id+"F1.wireOp",EDGE,"E10");var subQ1=sQuery(id+"F1.wireOp",EDGE,"E8");var subQ2=makeQuery(id+"F1.imprint","INTERSECT",VERTEX,{"derivedFrom":[subQ1,subQ0]});Q4=makeQuery(id+"F4.boolean.opBoolean","INTERSECT",EDGE,{"derivedFrom":[makeQuery(id+"F2.opExtrude","SWEPT_FACE",FACE,{"disambiguationData":[OSD([subQ0])]}),makeQuery(id+"F3.opExtrude","SWEPT_FACE",FACE,{"disambiguationData":[OSD([subQ1]),TDD([makeQuery(id+"F1.imprint","IMPRINT",EDGE,{"disambiguationData":[TD([[makeQuery(id+"F1.imprint","INTERSECT",VERTEX,{"derivedFrom":[sQuery(id+"F1.wireOp",EDGE,"E1"),subQ1]}),-1.0]])],"derivedFrom":subQ1}),makeQuery(id+"F1.imprint","IMPRINT",EDGE,{"disambiguationData":[TD([[subQ2,-1.0]])],"derivedFrom":subQ1})])]})]});}
            var Q5;
            {var subQ0=sQuery(id+"F1.wireOp",EDGE,"E10");var subQ1=sQuery(id+"F1.wireOp",EDGE,"E7");var subQ2=makeQuery(id+"F1.imprint","INTERSECT",VERTEX,{"derivedFrom":[subQ1,subQ0]});Q5=makeQuery(id+"F4.boolean.opBoolean","INTERSECT",EDGE,{"derivedFrom":[makeQuery(id+"F2.opExtrude","SWEPT_FACE",FACE,{"disambiguationData":[OSD([subQ0])]}),makeQuery(id+"F4.opPattern","COPY",FACE,{"derivedFrom":makeQuery(id+"F3.opExtrude","SWEPT_FACE",FACE,{"disambiguationData":[OSD([subQ1]),TDD([makeQuery(id+"F1.imprint","IMPRINT",EDGE,{"disambiguationData":[TD([[makeQuery(id+"F1.imprint","INTERSECT",VERTEX,{"derivedFrom":[sQuery(id+"F1.wireOp",EDGE,"E1"),subQ1]}),-1.0]])],"derivedFrom":subQ1}),makeQuery(id+"F1.imprint","IMPRINT",EDGE,{"disambiguationData":[TD([[subQ2,-1.0]])],"derivedFrom":subQ1})])]}),"instanceName":"1"})]});}
            var Q6;
            {var subQ0=sQuery(id+"F1.wireOp",EDGE,"E10");var subQ1=sQuery(id+"F1.wireOp",EDGE,"E8");var subQ2=makeQuery(id+"F1.imprint","INTERSECT",VERTEX,{"derivedFrom":[subQ1,subQ0]});Q6=makeQuery(id+"F4.boolean.opBoolean","INTERSECT",EDGE,{"derivedFrom":[makeQuery(id+"F2.opExtrude","SWEPT_FACE",FACE,{"disambiguationData":[OSD([subQ0])]}),makeQuery(id+"F4.opPattern","COPY",FACE,{"derivedFrom":makeQuery(id+"F3.opExtrude","SWEPT_FACE",FACE,{"disambiguationData":[OSD([subQ1]),TDD([makeQuery(id+"F1.imprint","IMPRINT",EDGE,{"disambiguationData":[TD([[makeQuery(id+"F1.imprint","INTERSECT",VERTEX,{"derivedFrom":[sQuery(id+"F1.wireOp",EDGE,"E1"),subQ1]}),-1.0]])],"derivedFrom":subQ1}),makeQuery(id+"F1.imprint","IMPRINT",EDGE,{"disambiguationData":[TD([[subQ2,-1.0]])],"derivedFrom":subQ1})])]}),"instanceName":"1"})]});}
            var Q7;
            {var subQ0=sQuery(id+"F1.wireOp",EDGE,"E10");var subQ1=sQuery(id+"F1.wireOp",EDGE,"E7");var subQ2=makeQuery(id+"F1.imprint","INTERSECT",VERTEX,{"derivedFrom":[subQ1,subQ0]});Q7=makeQuery(id+"F4.boolean.opBoolean","INTERSECT",EDGE,{"derivedFrom":[makeQuery(id+"F2.opExtrude","SWEPT_FACE",FACE,{"disambiguationData":[OSD([subQ0])]}),makeQuery(id+"F4.opPattern","COPY",FACE,{"derivedFrom":makeQuery(id+"F3.opExtrude","SWEPT_FACE",FACE,{"disambiguationData":[OSD([subQ1]),TDD([makeQuery(id+"F1.imprint","IMPRINT",EDGE,{"disambiguationData":[TD([[makeQuery(id+"F1.imprint","INTERSECT",VERTEX,{"derivedFrom":[sQuery(id+"F1.wireOp",EDGE,"E1"),subQ1]}),-1.0]])],"derivedFrom":subQ1}),makeQuery(id+"F1.imprint","IMPRINT",EDGE,{"disambiguationData":[TD([[subQ2,-1.0]])],"derivedFrom":subQ1})])]}),"instanceName":"2"})]});}
            fillet(context, id + "F16", {"entities" : qUnion([Q0, Q1, Q2, Q3, Q4, Q5, Q6, Q7]), "radius" : 1 * mm, "tangentPropagation" : true, "allowEdgeOverflow" : false});
        }
    });
